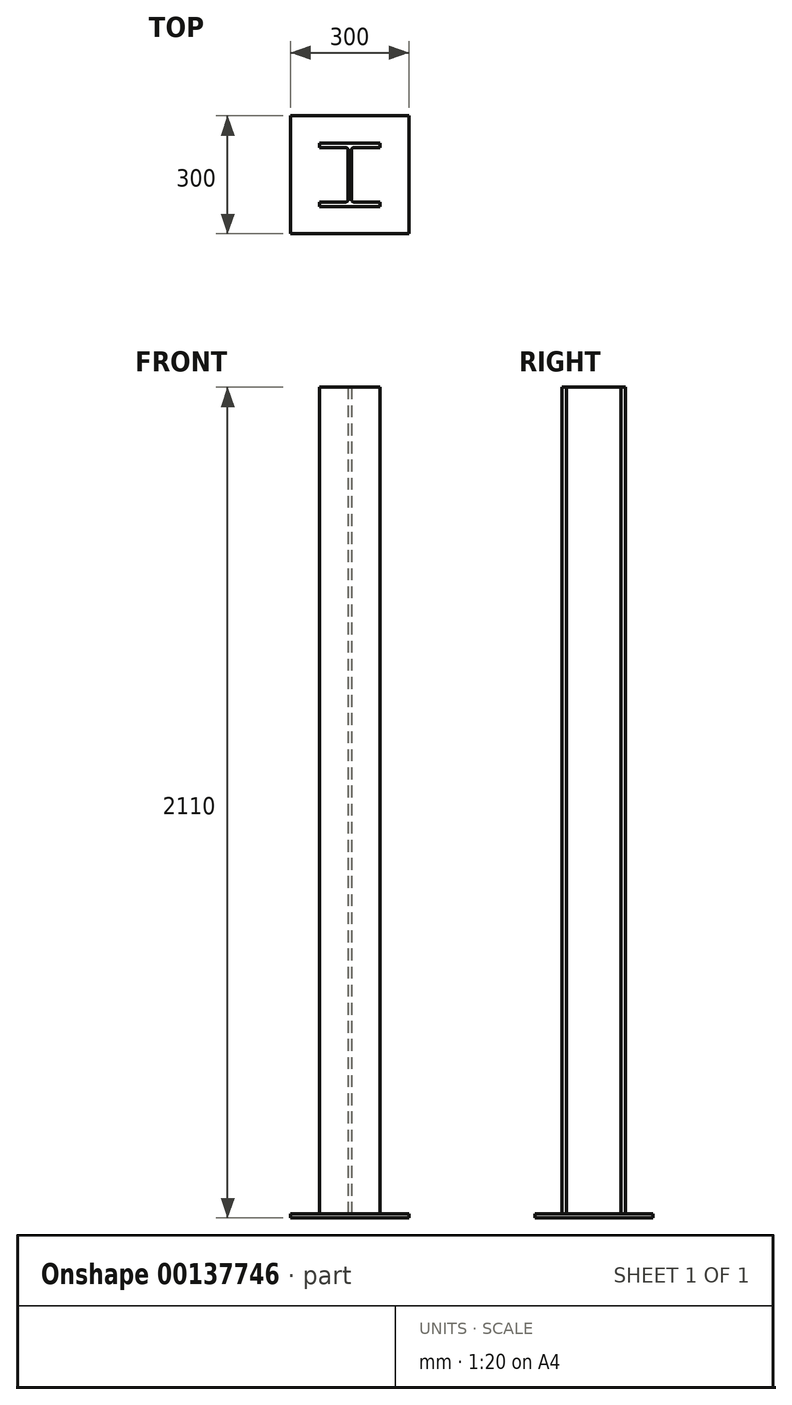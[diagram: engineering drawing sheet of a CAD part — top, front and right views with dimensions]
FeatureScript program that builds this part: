
annotation { "Feature Type Name" : "Feature", "Feature Type Description" : "" }
export const myFeature = defineFeature(function(context is Context, id is Id, definition is map)
    precondition{}
    {
        {
            var Q0;
            Q0=qCreatedBy(makeId("Top.planeOp"),FACE);
            var sketch = newSketch(context, id + "F0", { "sketchPlane" : qUnion([Q0])});
            skLineSegment(sketch, "E0.bottom", {"start": v(-150, -150) * mm, "end": v(150, -150) * mm});
            skLineSegment(sketch, "E0.top", {"start": v(-150, 150) * mm, "end": v(150, 150) * mm});
            skLineSegment(sketch, "E0.left", {"start": v(-150, -150) * mm, "end": v(-150, 150) * mm});
            skLineSegment(sketch, "E0.right", {"start": v(150, -150) * mm, "end": v(150, 150) * mm});
            skPoint(sketch, "E0.middle", {"position": v(0, 0) * mm});
            skSolve(sketch);
        }
        {
            var Q0;
            Q0=makeQuery(id+"F0.imprint","IMPRINT",FACE,{"disambiguationData":[TD([[makeQuery(id+"F0.imprint","IMPRINT",EDGE,{"derivedFrom":sQuery(id+"F0.wireOp",EDGE,"E0.bottom")}),1.0]])]});
            extrude(context, id + "F1", {"entities" : qUnion([Q0]), "depth" : 10 * mm});
        }
        {
            var Q0;
            Q0=makeQuery(id+"F1.opExtrude","CAP_FACE",FACE,{"disambiguationData":[OSD([sQuery(id+"F0.wireOp",EDGE,"E0.bottom"),sQuery(id+"F0.wireOp",EDGE,"E0.top"),sQuery(id+"F0.wireOp",EDGE,"E0.left"),sQuery(id+"F0.wireOp",EDGE,"E0.right")])],"isStart":false});
            var sketch = newSketch(context, id + "F2", { "sketchPlane" : qUnion([Q0])});
            skLineSegment(sketch, "E1", {"start": v(-77.2, 80.9) * mm, "end": v(-77.2, 69.4) * mm});
            skLineSegment(sketch, "E2", {"start": v(-77.2, 69.4) * mm, "end": v(-11.6, 69.4) * mm});
            skArc(sketch, "E3", {"start": v(-11.6, 69.4) * mm, "mid": v(-6.23, 67.17) * mm, "end": v(-4, 61.8) * mm});
            skLineSegment(sketch, "E4", {"start": v(-4, 61.8) * mm, "end": v(-4, -61.8) * mm});
            skArc(sketch, "E5", {"start": v(-4, -61.8) * mm, "mid": v(-6.23, -67.17) * mm, "end": v(-11.6, -69.4) * mm});
            skLineSegment(sketch, "E6", {"start": v(-11.6, -69.4) * mm, "end": v(-77.2, -69.4) * mm});
            skLineSegment(sketch, "E7", {"start": v(-77.2, -69.4) * mm, "end": v(-77.2, -80.9) * mm});
            skLineSegment(sketch, "E8", {"start": v(-77.2, -80.9) * mm, "end": v(77.2, -80.9) * mm});
            skLineSegment(sketch, "E9", {"start": v(77.2, -80.9) * mm, "end": v(77.2, -69.4) * mm});
            skLineSegment(sketch, "E10", {"start": v(77.2, -69.4) * mm, "end": v(11.6, -69.4) * mm});
            skArc(sketch, "E11", {"start": v(11.6, -69.4) * mm, "mid": v(6.23, -67.17) * mm, "end": v(4, -61.8) * mm});
            skLineSegment(sketch, "E12", {"start": v(4, -61.8) * mm, "end": v(4, 61.8) * mm});
            skArc(sketch, "E13", {"start": v(4, 61.8) * mm, "mid": v(6.23, 67.17) * mm, "end": v(11.6, 69.4) * mm});
            skLineSegment(sketch, "E14", {"start": v(11.6, 69.4) * mm, "end": v(77.2, 69.4) * mm});
            skLineSegment(sketch, "E15", {"start": v(77.2, 69.4) * mm, "end": v(77.2, 80.9) * mm});
            skLineSegment(sketch, "E16", {"start": v(77.2, 80.9) * mm, "end": v(-77.2, 80.9) * mm});
            skSolve(sketch);
        }
        {
            var Q0;
            Q0=makeQuery(id+"F2.imprint","IMPRINT",FACE,{"disambiguationData":[TD([[makeQuery(id+"F2.imprint","IMPRINT",EDGE,{"derivedFrom":sQuery(id+"F2.wireOp",EDGE,"E1")}),1.0]])]});
            extrude(context, id + "F3", {"entities" : qUnion([Q0]), "operationType" : NewBodyOperationType.ADD, "depth" : 2100 * mm});
        }
    });
